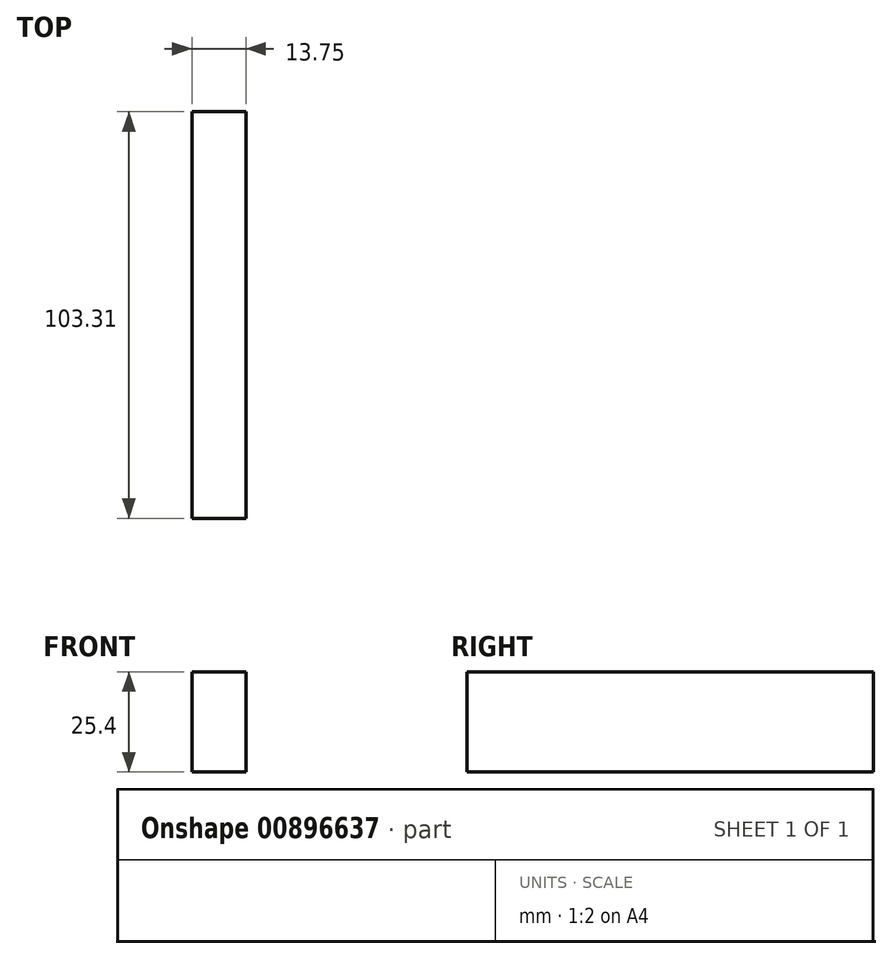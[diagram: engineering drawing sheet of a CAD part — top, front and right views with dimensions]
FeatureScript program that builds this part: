
annotation { "Feature Type Name" : "Feature", "Feature Type Description" : "" }
export const myFeature = defineFeature(function(context is Context, id is Id, definition is map)
    precondition{}
    {
        {
            var Q0;
            Q0=qCreatedBy(makeId("Top.planeOp"),FACE);
            var sketch = newSketch(context, id + "F0", { "sketchPlane" : qUnion([Q0])});
            skLineSegment(sketch, "E0.bottom", {"start": v(5.44, 61.2) * mm, "end": v(-8.3, 61.2) * mm});
            skLineSegment(sketch, "E0.top", {"start": v(5.44, -42.1) * mm, "end": v(-8.3, -42.1) * mm});
            skLineSegment(sketch, "E0.left", {"start": v(5.44, 61.2) * mm, "end": v(5.44, -42.1) * mm});
            skLineSegment(sketch, "E0.right", {"start": v(-8.3, 61.2) * mm, "end": v(-8.3, -42.1) * mm});
            skSolve(sketch);
        }
        {
            var Q0;
            Q0 = qSketchRegion(id + "F0", true);
            extrude(context, id + "F1", {"entities" : qUnion([Q0]), "depth" : 25.4 * mm, "offsetDistance" : 25.4 * mm});
        }
    });
